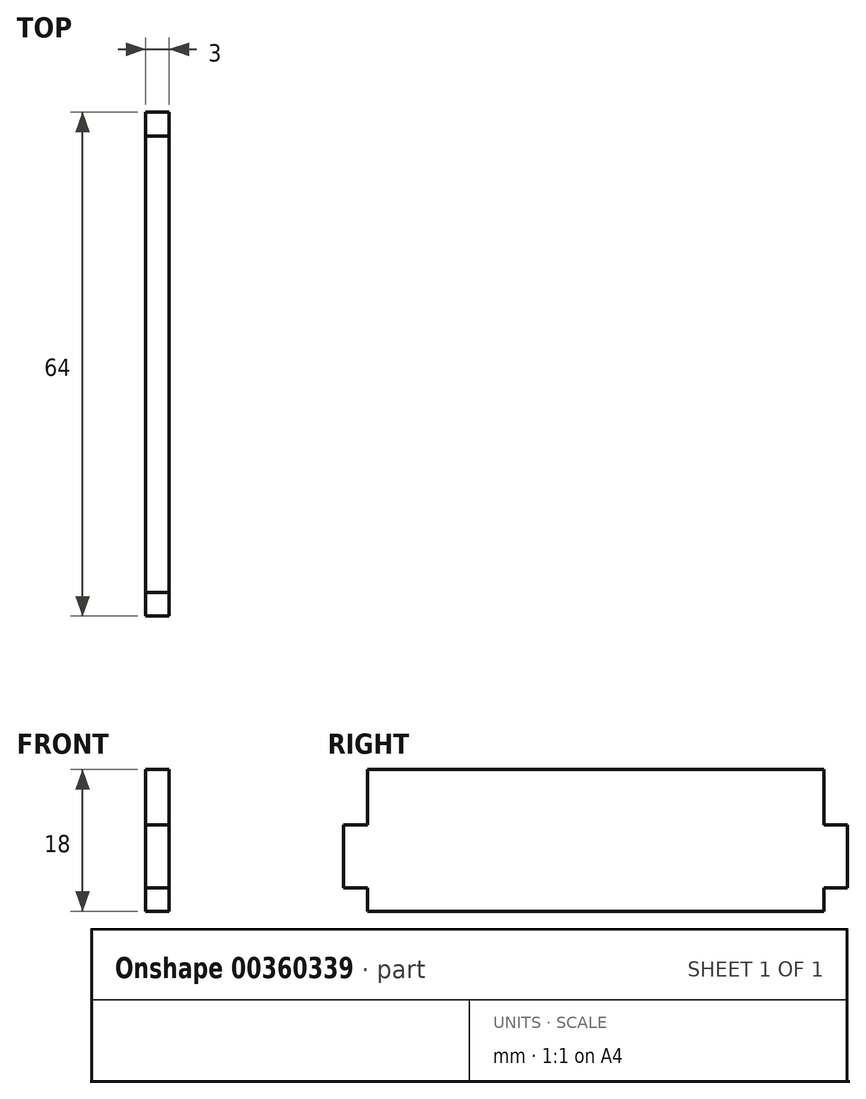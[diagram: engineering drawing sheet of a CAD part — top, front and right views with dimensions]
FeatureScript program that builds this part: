
annotation { "Feature Type Name" : "Feature", "Feature Type Description" : "" }
export const myFeature = defineFeature(function(context is Context, id is Id, definition is map)
    precondition{}
    {
        {
            var Q0;
            Q0=qCreatedBy(makeId("Right.planeOp"),FACE);
            var sketch = newSketch(context, id + "F0", { "sketchPlane" : qUnion([Q0])});
            skLineSegment(sketch, "E0", {"start": v(-32, 0) * mm, "end": v(-32, 4) * mm});
            skLineSegment(sketch, "E1", {"start": v(-32, 4) * mm, "end": v(-29, 4) * mm});
            skLineSegment(sketch, "E2", {"start": v(-29, 4) * mm, "end": v(-29, 11) * mm});
            skLineSegment(sketch, "E3", {"start": v(-29, 11) * mm, "end": v(0, 11) * mm});
            skLineSegment(sketch, "E4", {"start": v(-32, 0) * mm, "end": v(-32, -4) * mm});
            skLineSegment(sketch, "E5", {"start": v(-32, -4) * mm, "end": v(-29, -4) * mm});
            skLineSegment(sketch, "E6", {"start": v(-29, -4) * mm, "end": v(-29, -7) * mm});
            skLineSegment(sketch, "E7", {"start": v(-29, -7) * mm, "end": v(0, -7) * mm});
            skLineSegment(sketch, "E8.MirrorCS", {"start": v(29, -4) * mm, "end": v(29, -7) * mm});
            skLineSegment(sketch, "E9.MirrorCS", {"start": v(32, -4) * mm, "end": v(29, -4) * mm});
            skLineSegment(sketch, "E10.MirrorCS", {"start": v(32, 4) * mm, "end": v(29, 4) * mm});
            skLineSegment(sketch, "E11.MirrorCS", {"start": v(32, 0) * mm, "end": v(32, 4) * mm});
            skLineSegment(sketch, "E12.MirrorCS", {"start": v(29, -7) * mm, "end": v(0, -7) * mm});
            skLineSegment(sketch, "E13.MirrorCS", {"start": v(29, 4) * mm, "end": v(29, 11) * mm});
            skLineSegment(sketch, "E14.MirrorCS", {"start": v(32, 0) * mm, "end": v(32, -4) * mm});
            skLineSegment(sketch, "E15.MirrorCS", {"start": v(29, 11) * mm, "end": v(0, 11) * mm});
            skSolve(sketch);
        }
        {
            var Q0;
            Q0 = qSketchRegion(id + "F0", true);
            extrude(context, id + "F1", {"entities" : qUnion([Q0]), "depth" : 3 * mm});
        }
    });
